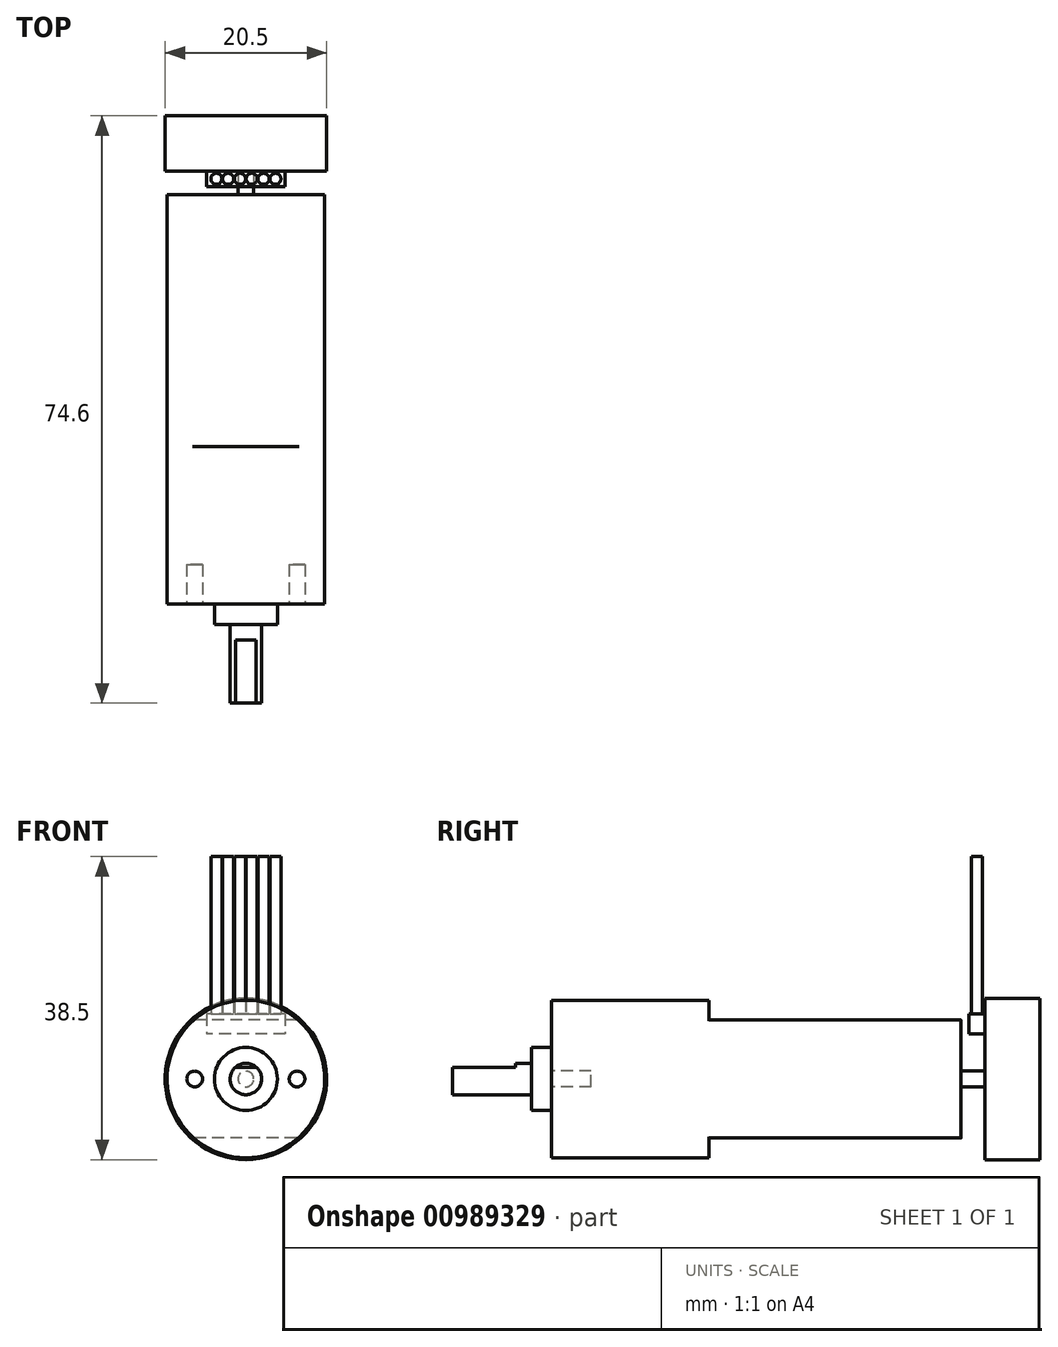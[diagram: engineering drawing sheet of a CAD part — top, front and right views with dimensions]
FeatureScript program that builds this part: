
annotation { "Feature Type Name" : "Feature", "Feature Type Description" : "" }
export const myFeature = defineFeature(function(context is Context, id is Id, definition is map)
    precondition{}
    {
        {
            var Q0;
            Q0=qCreatedBy(makeId("Front.planeOp"),FACE);
            var sketch = newSketch(context, id + "F0", { "sketchPlane" : qUnion([Q0])});
            skCircle(sketch, "E0", {"center": v(0, 0) * mm, "radius": 10 * mm});
            skSolve(sketch);
        }
        {
            var Q0;
            Q0=qSketchRegion(id+"F0",true);
            extrude(context, id + "F1", {"entities" : qUnion([Q0]), "depth" : 20 * mm, "offsetDistance" : 25 * mm});
        }
        {
            var Q0;
            Q0=makeQuery(id+"F1.opExtrude","CAP_FACE",FACE,{"disambiguationData":[OSD([sQuery(id+"F0.wireOp",EDGE,"E0")])],"isStart":false});
            var sketch = newSketch(context, id + "F2", { "sketchPlane" : qUnion([Q0])});
            skCircle(sketch, "E1", {"center": v(0, 0) * mm, "radius": 4 * mm});
            skSolve(sketch);
        }
        {
            var Q0;
            Q0=qSketchRegion(id+"F2",true);
            extrude(context, id + "F3", {"entities" : qUnion([Q0]), "operationType" : NewBodyOperationType.ADD, "depth" : 2.6 * mm, "offsetDistance" : 25 * mm});
        }
        {
            var Q0;
            Q0=makeQuery(id+"F3.opExtrude","CAP_FACE",FACE,{"disambiguationData":[OSD([sQuery(id+"F2.wireOp",EDGE,"E1")])],"isStart":false});
            var sketch = newSketch(context, id + "F4", { "sketchPlane" : qUnion([Q0])});
            skCircle(sketch, "E2", {"center": v(0, 0) * mm, "radius": 2 * mm});
            skSolve(sketch);
        }
        {
            var Q0;
            Q0=qSketchRegion(id+"F4",true);
            extrude(context, id + "F5", {"entities" : qUnion([Q0]), "operationType" : NewBodyOperationType.ADD, "depth" : 10 * mm, "offsetDistance" : 25 * mm});
        }
        {
            var Q0;
            Q0=makeQuery(id+"F5.opExtrude","CAP_FACE",FACE,{"disambiguationData":[OSD([sQuery(id+"F4.wireOp",EDGE,"E2")])],"isStart":false});
            var sketch = newSketch(context, id + "F6", { "sketchPlane" : qUnion([Q0])});
            skLineSegment(sketch, "E3", {"start": v(-1.32, 1.5) * mm, "end": v(1.32, 1.5) * mm});
            skArc(sketch, "E4", {"start": v(-1.32, 1.5) * mm, "mid": v(0, 2) * mm, "end": v(1.32, 1.5) * mm});
            skSolve(sketch);
        }
        {
            var Q0;
            Q0=qSketchRegion(id+"F6",true);
            extrude(context, id + "F7", {"entities" : qUnion([Q0]), "operationType" : NewBodyOperationType.REMOVE, "oppositeDirection" : true, "depth" : 8 * mm, "offsetDistance" : 25 * mm});
        }
        {
            var Q0;
            Q0=makeQuery(id+"F1.opExtrude","CAP_FACE",FACE,{"disambiguationData":[OSD([sQuery(id+"F0.wireOp",EDGE,"E0")])],"isStart":false});
            var sketch = newSketch(context, id + "F8", { "sketchPlane" : qUnion([Q0])});
            skCircle(sketch, "E5", {"center": v(-6.5, 0) * mm, "radius": 1 * mm});
            skCircle(sketch, "E6.MirrorC", {"center": v(6.5, 0) * mm, "radius": 1 * mm});
            skSolve(sketch);
        }
        {
            var Q0;
            Q0=qSketchRegion(id+"F8",true);
            extrude(context, id + "F9", {"entities" : qUnion([Q0]), "operationType" : NewBodyOperationType.REMOVE, "oppositeDirection" : true, "depth" : 5 * mm, "offsetDistance" : 25 * mm});
        }
        {
            var Q0;
            Q0=makeQuery(id+"F1.opExtrude","CAP_FACE",FACE,{"disambiguationData":[OSD([sQuery(id+"F0.wireOp",EDGE,"E0")])],"isStart":true});
            var sketch = newSketch(context, id + "F10", { "sketchPlane" : qUnion([Q0])});
            skLineSegment(sketch, "E7", {"start": v(-6.61, 7.5) * mm, "end": v(6.61, 7.5) * mm});
            skLineSegment(sketch, "E8.MirrorCS", {"start": v(-6.61, -7.5) * mm, "end": v(6.61, -7.5) * mm});
            skArc(sketch, "E9", {"start": v(-6.61, 7.5) * mm, "mid": v(-10, 0) * mm, "end": v(-6.61, -7.5) * mm});
            skArc(sketch, "E10.trimOffspring", {"start": v(6.61, -7.5) * mm, "mid": v(10, 0) * mm, "end": v(6.61, 7.5) * mm});
            skSolve(sketch);
        }
        {
            var Q0;
            Q0=qSketchRegion(id+"F10",true);
            extrude(context, id + "F11", {"entities" : qUnion([Q0]), "operationType" : NewBodyOperationType.ADD, "depth" : 32 * mm, "offsetDistance" : 25 * mm});
        }
        {
            var Q0;
            Q0=makeQuery(id+"F11.opExtrude","SWEPT_EDGE",EDGE,{"disambiguationData":[OSD([sQuery(id+"F0.wireOp",EDGE,"E0"),sQuery(id+"F10.wireOp",EDGE,"E7"),sQuery(id+"F10.wireOp",EDGE,"E9")])]});
            var Q1;
            Q1=makeQuery(id+"F11.opExtrude","SWEPT_EDGE",EDGE,{"disambiguationData":[OSD([sQuery(id+"F0.wireOp",EDGE,"E0"),sQuery(id+"F10.wireOp",EDGE,"E7"),sQuery(id+"F10.wireOp",EDGE,"E10.trimOffspring")])]});
            var Q2;
            Q2=makeQuery(id+"F11.opExtrude","SWEPT_EDGE",EDGE,{"disambiguationData":[OSD([sQuery(id+"F0.wireOp",EDGE,"E0"),sQuery(id+"F10.wireOp",EDGE,"E8.MirrorCS"),sQuery(id+"F10.wireOp",EDGE,"E10.trimOffspring")])]});
            var Q3;
            Q3=makeQuery(id+"F11.opExtrude","SWEPT_EDGE",EDGE,{"disambiguationData":[OSD([sQuery(id+"F0.wireOp",EDGE,"E0"),sQuery(id+"F10.wireOp",EDGE,"E8.MirrorCS"),sQuery(id+"F10.wireOp",EDGE,"E9")])]});
            fillet(context, id + "F12", {"entities" : qUnion([Q0, Q1, Q2, Q3]), "radius" : 0.5 * mm, "tangentPropagation" : true, "allowEdgeOverflow" : false});
        }
        {
            var Q0;
            Q0=makeQuery(id+"F11.opExtrude","CAP_FACE",FACE,{"disambiguationData":[OSD([sQuery(id+"F10.wireOp",EDGE,"E7"),sQuery(id+"F10.wireOp",EDGE,"E8.MirrorCS"),sQuery(id+"F10.wireOp",EDGE,"E9"),sQuery(id+"F10.wireOp",EDGE,"E10.trimOffspring")])],"isStart":false});
            var sketch = newSketch(context, id + "F13", { "sketchPlane" : qUnion([Q0])});
            skCircle(sketch, "E11", {"center": v(0, 0) * mm, "radius": 1 * mm});
            skSolve(sketch);
        }
        {
            var Q0;
            Q0=qSketchRegion(id+"F13",true);
            extrude(context, id + "F14", {"entities" : qUnion([Q0]), "operationType" : NewBodyOperationType.ADD, "depth" : 3 * mm, "offsetDistance" : 25 * mm});
        }
        {
            var Q0;
            Q0=makeQuery(id+"F14.opExtrude","CAP_FACE",FACE,{"disambiguationData":[OSD([sQuery(id+"F13.wireOp",EDGE,"E11")])],"isStart":false});
            var sketch = newSketch(context, id + "F15", { "sketchPlane" : qUnion([Q0])});
            skCircle(sketch, "E12", {"center": v(0, 0) * mm, "radius": 10.25 * mm});
            skSolve(sketch);
        }
        {
            var Q0;
            Q0=qSketchRegion(id+"F15",true);
            extrude(context, id + "F16", {"entities" : qUnion([Q0]), "operationType" : NewBodyOperationType.ADD, "depth" : 7 * mm, "offsetDistance" : 25 * mm});
        }
        {
            var Q0;
            Q0=makeQuery(id+"F16.opExtrude","CAP_FACE",FACE,{"disambiguationData":[OSD([sQuery(id+"F15.wireOp",EDGE,"E12")])],"isStart":true});
            var sketch = newSketch(context, id + "F17", { "sketchPlane" : qUnion([Q0])});
            skLineSegment(sketch, "E13.bottom", {"start": v(5, 8.25) * mm, "end": v(-5, 8.25) * mm});
            skLineSegment(sketch, "E13.top", {"start": v(5, 5.75) * mm, "end": v(-5, 5.75) * mm});
            skLineSegment(sketch, "E13.left", {"start": v(5, 8.25) * mm, "end": v(5, 5.75) * mm});
            skLineSegment(sketch, "E13.right", {"start": v(-5, 8.25) * mm, "end": v(-5, 5.75) * mm});
            skPoint(sketch, "E13.middle", {"position": v(0, 7) * mm});
            skSolve(sketch);
        }
        {
            var Q0;
            Q0=qSketchRegion(id+"F17",true);
            extrude(context, id + "F18", {"entities" : qUnion([Q0]), "operationType" : NewBodyOperationType.ADD, "depth" : 2 * mm, "offsetDistance" : 25 * mm});
        }
        {
            var Q0;
            Q0=makeQuery(id+"F18.opExtrude","SWEPT_FACE",FACE,{"disambiguationData":[OSD([sQuery(id+"F17.wireOp",EDGE,"E13.bottom")])]});
            var sketch = newSketch(context, id + "F19", { "sketchPlane" : qUnion([Q0])});
            skCircle(sketch, "E14", {"center": v(-3.75, 34) * mm, "radius": 0.7 * mm});
            skCircle(sketch, "E15.1.0.0", {"center": v(-2.25, 34) * mm, "radius": 0.7 * mm});
            skCircle(sketch, "E15.2.0.0", {"center": v(-0.75, 34) * mm, "radius": 0.7 * mm});
            skLineSegment(sketch, "E15.direction1", {"start": v(-3.75, 34) * mm, "end": v(-2.25, 34) * mm, "construction": true});
            skCircle(sketch, "E16.0.3.0", {"center": v(0.75, 34) * mm, "radius": 0.7 * mm});
            skCircle(sketch, "E16.0.4.0", {"center": v(2.25, 34) * mm, "radius": 0.7 * mm});
            skCircle(sketch, "E16.0.5.0", {"center": v(3.75, 34) * mm, "radius": 0.7 * mm});
            skPoint(sketch, "E17", {"position": v(0, 34) * mm});
            skSolve(sketch);
        }
        {
            var Q0;
            Q0=qSketchRegion(id+"F19",true);
            extrude(context, id + "F20", {"entities" : qUnion([Q0]), "operationType" : NewBodyOperationType.ADD, "depth" : 20 * mm, "offsetDistance" : 25 * mm});
        }
    });
